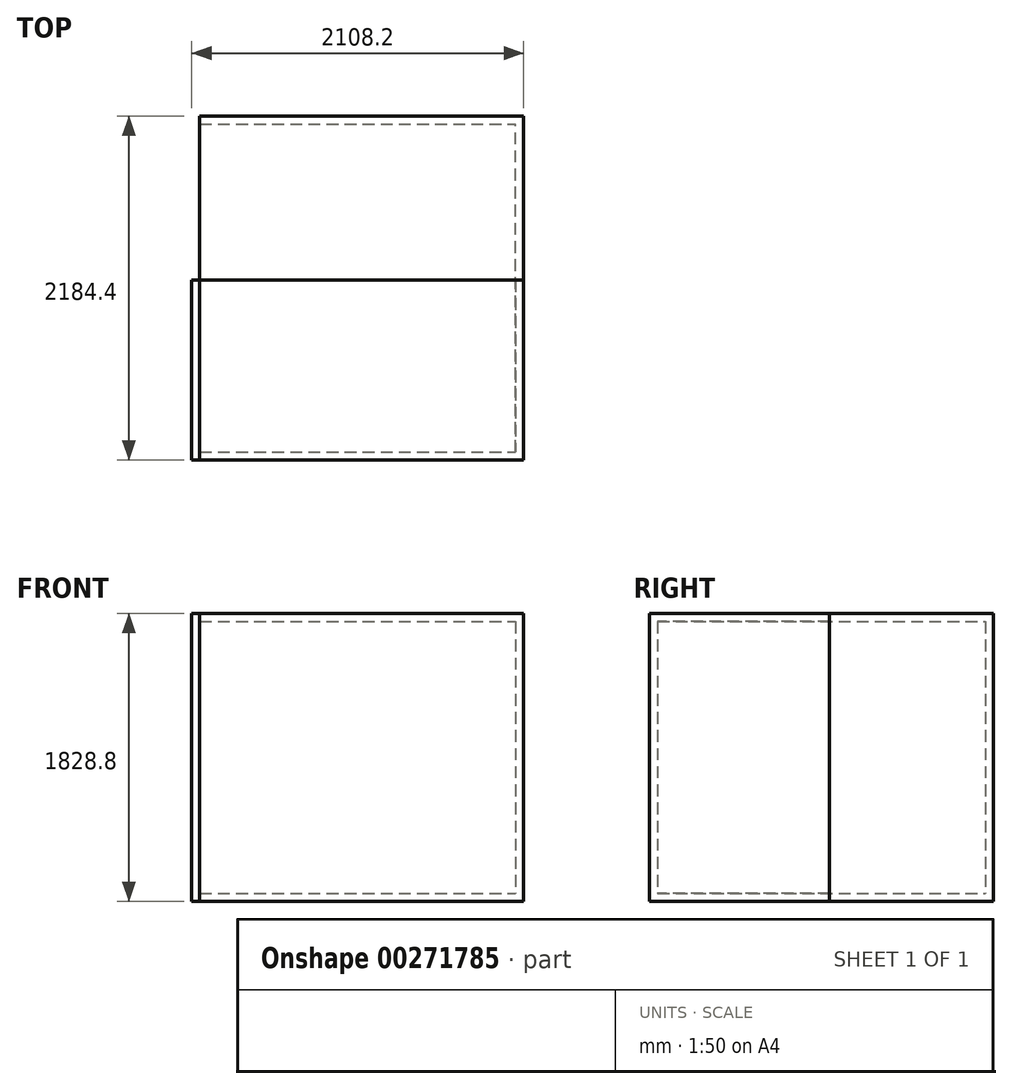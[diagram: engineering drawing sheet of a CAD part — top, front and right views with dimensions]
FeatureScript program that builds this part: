
annotation { "Feature Type Name" : "Feature", "Feature Type Description" : "" }
export const myFeature = defineFeature(function(context is Context, id is Id, definition is map)
    precondition{}
    {
        {
            var Q0;
            Q0=qCreatedBy(makeId("Front.planeOp"),FACE);
            var sketch = newSketch(context, id + "F0", { "sketchPlane" : qUnion([Q0])});
            skLineSegment(sketch, "E0.bottom", {"start": v(-48.64, 35.6) * mm, "end": v(48.64, 35.6) * mm});
            skLineSegment(sketch, "E0.top", {"start": v(-48.64, -35.6) * mm, "end": v(48.64, -35.6) * mm});
            skLineSegment(sketch, "E0.left", {"start": v(-48.64, 35.6) * mm, "end": v(-48.64, -35.6) * mm});
            skLineSegment(sketch, "E0.right", {"start": v(48.64, 35.6) * mm, "end": v(48.64, -35.6) * mm});
            skPoint(sketch, "E0.middle", {"position": v(0, 0) * mm});
            skSolve(sketch);
        }
        {
            var Q0;
            Q0=makeQuery(id+"F0.imprint","IMPRINT",FACE,{"disambiguationData":[TD([[makeQuery(id+"F0.imprint","IMPRINT",EDGE,{"derivedFrom":sQuery(id+"F0.wireOp",EDGE,"E0.bottom")}),-1.0]])]});
            extrude(context, id + "F1", {"entities" : qUnion([Q0]), "endBound" : BoundingType.SYMMETRIC, "depth" : 2184.4 * mm});
        }
        {
            var Q0;
            Q0=makeQuery(id+"F1.opExtrude","SWEPT_FACE",FACE,{"disambiguationData":[OSD([sQuery(id+"F0.wireOp",EDGE,"E0.left")])]});
            extrude(context, id + "F2", {"entities" : qUnion([Q0]), "operationType" : NewBodyOperationType.ADD, "endBound" : BoundingType.SYMMETRIC, "depth" : 2057.4 * mm});
        }
        {
            var Q0;
            {var subQ0=sQuery(id+"F0.wireOp",EDGE,"E0.bottom");Q0=makeQuery(id+"F2.boolean.opBoolean","MERGE",FACE,{"derivedFrom":[makeQuery(id+"F1.opExtrude","SWEPT_FACE",FACE,{"disambiguationData":[OSD([subQ0])]}),makeQuery(id+"F2.opExtrude","SWEPT_FACE",FACE,{"disambiguationData":[OSD([subQ0,sQuery(id+"F0.wireOp",EDGE,"E0.left")])]})]});}
            extrude(context, id + "F3", {"entities" : qUnion([Q0]), "operationType" : NewBodyOperationType.ADD, "endBound" : BoundingType.SYMMETRIC, "depth" : 1828.8 * mm});
        }
        {
            var Q0;
            {var subQ0=sQuery(id+"F0.wireOp",EDGE,"E0.left");var subQ1=sQuery(id+"F0.wireOp",EDGE,"E0.bottom");Q0=makeQuery(id+"F3.boolean.opBoolean","MERGE",FACE,{"derivedFrom":[makeQuery(id+"F2.opExtrude","CAP_FACE",FACE,{"disambiguationData":[OSD([subQ0])],"isStart":false}),makeQuery(id+"F3.opExtrude","SWEPT_FACE",FACE,{"disambiguationData":[OSD([subQ1,subQ0]),TDD([makeQuery(id+"F2.opExtrude","CAP_EDGE",EDGE,{"disambiguationData":[OSD([subQ1,subQ0])],"isStart":false})])]})]});}
            shell(context, id + "F4", {"entities" : qUnion([Q0]), "thickness" : 50.8 * mm});
        }
        {
            var Q0;
            {var subQ0=sQuery(id+"F0.wireOp",EDGE,"E0.left");var subQ1=sQuery(id+"F0.wireOp",EDGE,"E0.bottom");var subQ2=sQuery(id+"F0.wireOp",EDGE,"E0.right");var subQ3=sQuery(id+"F0.wireOp",EDGE,"E0.top");Q0=makeQuery(id+"F4.opShell","OFFSET_FACE",FACE,{"disambiguationData":[OSD([subQ1,subQ3,subQ0,subQ2]),TDD([makeQuery(id+"F3.boolean.opBoolean","MERGE",FACE,{"derivedFrom":[makeQuery(id+"F2.boolean.opBoolean","MERGE",FACE,{"derivedFrom":[makeQuery(id+"F1.opExtrude","CAP_FACE",FACE,{"disambiguationData":[OSD([subQ1,subQ3,subQ0,subQ2])],"isStart":false}),makeQuery(id+"F2.opExtrude","SWEPT_FACE",FACE,{"disambiguationData":[OSD([subQ0]),TDD([makeQuery(id+"F1.opExtrude","CAP_EDGE",EDGE,{"disambiguationData":[OSD([subQ0])],"isStart":false})])]})]}),makeQuery(id+"F3.opExtrude","SWEPT_FACE",FACE,{"disambiguationData":[OSD([subQ1,subQ0]),TDD([makeQuery(id+"F2.boolean.opBoolean","MERGE",EDGE,{"derivedFrom":[makeQuery(id+"F1.opExtrude","CAP_EDGE",EDGE,{"disambiguationData":[OSD([subQ1])],"isStart":false}),makeQuery(id+"F2.opExtrude","SWEPT_EDGE",EDGE,{"disambiguationData":[OSD([subQ1,subQ0]),TDD([makeQuery(id+"F1.opExtrude","CAP_VERTEX",VERTEX,{"disambiguationData":[OSD([subQ1,subQ0])],"isStart":false})])]})]})])]})]})])]});}
            extrude(context, id + "F5", {"entities" : qUnion([Q0]), "depth" : 1092.2 * mm});
        }
        {
            var Q0;
            Q0=makeQuery(id+"F5.opExtrude","CAP_FACE",FACE,{"disambiguationData":[OSD([sQuery(id+"F0.wireOp",EDGE,"E0.bottom"),sQuery(id+"F0.wireOp",EDGE,"E0.top"),sQuery(id+"F0.wireOp",EDGE,"E0.left"),sQuery(id+"F0.wireOp",EDGE,"E0.right")])],"isStart":false});
            shell(context, id + "F6", {"entities" : qUnion([Q0]), "thickness" : 50.8 * mm, "oppositeDirection" : true});
        }
    });
